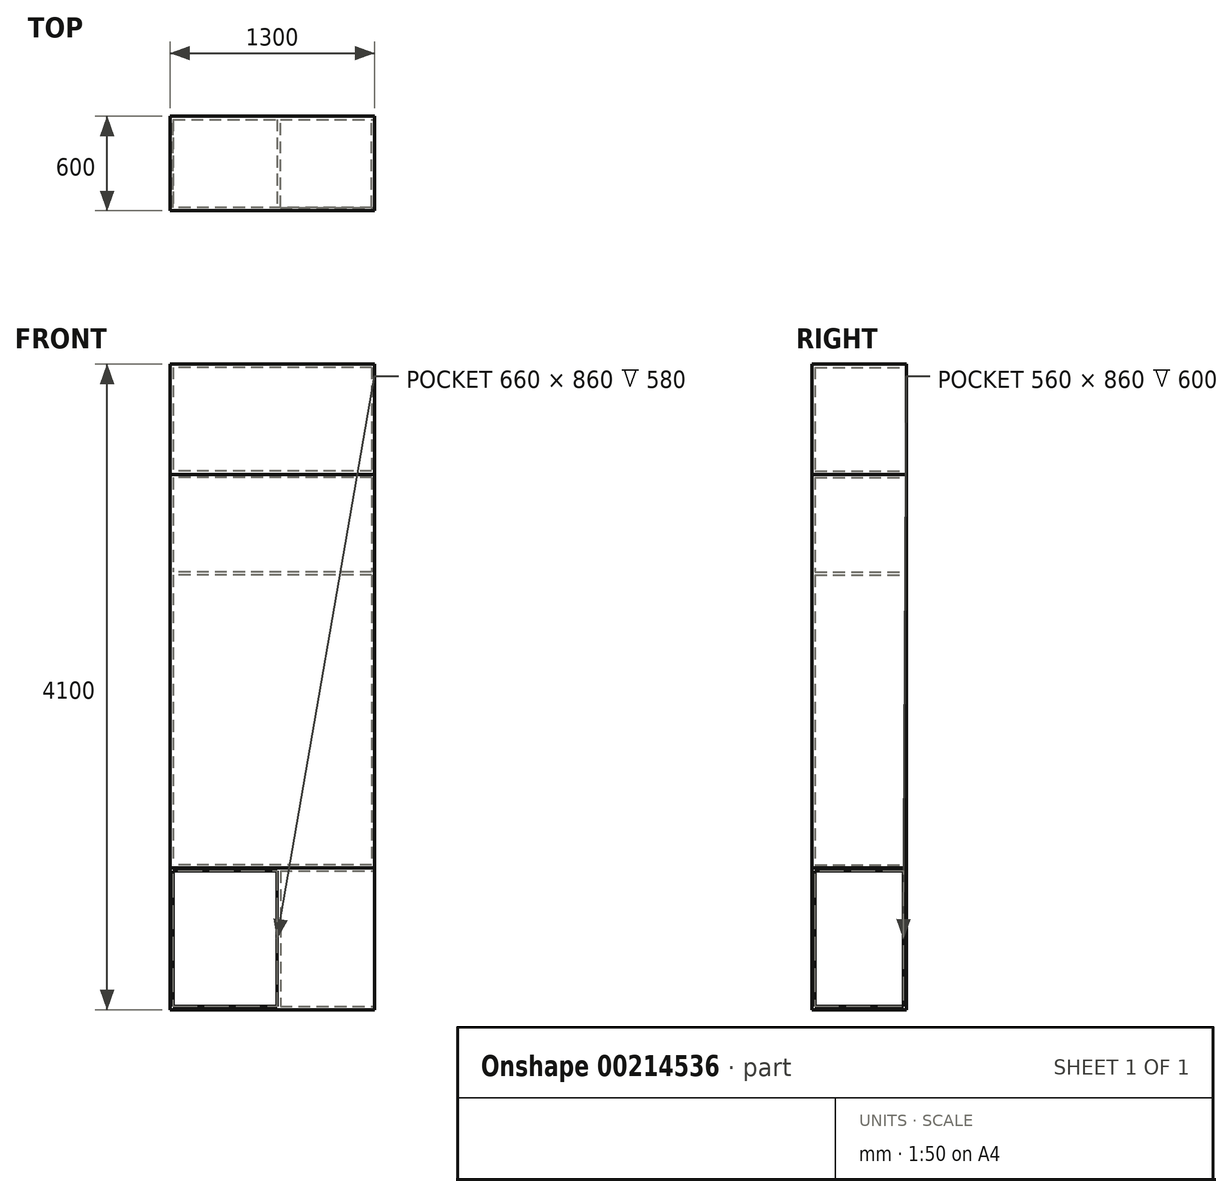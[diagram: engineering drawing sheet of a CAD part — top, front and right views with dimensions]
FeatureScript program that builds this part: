
annotation { "Feature Type Name" : "Feature", "Feature Type Description" : "" }
export const myFeature = defineFeature(function(context is Context, id is Id, definition is map)
    precondition{}
    {
        {
            var Q0;
            Q0=qCreatedBy(makeId("Top.planeOp"),FACE);
            var sketch = newSketch(context, id + "F0", { "sketchPlane" : qUnion([Q0])});
            skLineSegment(sketch, "E0.bottom", {"start": v(0, 0) * mm, "end": v(1300, 0) * mm});
            skLineSegment(sketch, "E0.top", {"start": v(0, 600) * mm, "end": v(1300, 600) * mm});
            skLineSegment(sketch, "E0.left", {"start": v(0, 0) * mm, "end": v(0, 600) * mm});
            skLineSegment(sketch, "E0.right", {"start": v(1300, 0) * mm, "end": v(1300, 600) * mm});
            skSolve(sketch);
        }
        {
            var Q0;
            Q0=makeQuery(id+"F0.imprint","IMPRINT",FACE,{"disambiguationData":[TD([[makeQuery(id+"F0.imprint","IMPRINT",EDGE,{"derivedFrom":sQuery(id+"F0.wireOp",EDGE,"E0.bottom")}),1.0]])]});
            extrude(context, id + "F1", {"entities" : qUnion([Q0]), "depth" : 900 * mm});
        }
        {
            var Q0;
            Q0=makeQuery(id+"F1.opExtrude","SWEPT_FACE",FACE,{"disambiguationData":[OSD([sQuery(id+"F0.wireOp",EDGE,"E0.right")])]});
            var sketch = newSketch(context, id + "F2", { "sketchPlane" : qUnion([Q0])});
            skLineSegment(sketch, "E1.bottom", {"start": v(20, 880) * mm, "end": v(580, 880) * mm});
            skLineSegment(sketch, "E1.top", {"start": v(20, 20) * mm, "end": v(580, 20) * mm});
            skLineSegment(sketch, "E1.left", {"start": v(20, 880) * mm, "end": v(20, 20) * mm});
            skLineSegment(sketch, "E1.right", {"start": v(580, 880) * mm, "end": v(580, 20) * mm});
            skSolve(sketch);
        }
        {
            var Q0;
            Q0 = qSketchRegion(id + "F2", true);
            extrude(context, id + "F3", {"entities" : qUnion([Q0]), "operationType" : NewBodyOperationType.REMOVE, "oppositeDirection" : true, "depth" : 600 * mm});
        }
        {
            var Q0;
            Q0=makeQuery(id+"F1.opExtrude","SWEPT_FACE",FACE,{"disambiguationData":[OSD([sQuery(id+"F0.wireOp",EDGE,"E0.bottom")])]});
            var sketch = newSketch(context, id + "F4", { "sketchPlane" : qUnion([Q0])});
            skLineSegment(sketch, "E2.bottom", {"start": v(20, 880) * mm, "end": v(680, 880) * mm});
            skLineSegment(sketch, "E2.top", {"start": v(20, 20) * mm, "end": v(680, 20) * mm});
            skLineSegment(sketch, "E2.left", {"start": v(20, 880) * mm, "end": v(20, 20) * mm});
            skLineSegment(sketch, "E2.right", {"start": v(680, 880) * mm, "end": v(680, 20) * mm});
            skSolve(sketch);
        }
        {
            var Q0;
            Q0 = qSketchRegion(id + "F4", true);
            extrude(context, id + "F5", {"entities" : qUnion([Q0]), "operationType" : NewBodyOperationType.REMOVE, "oppositeDirection" : true, "depth" : 580 * mm});
        }
        {
            var Q0;
            Q0=makeQuery(id+"F1.opExtrude","CAP_FACE",FACE,{"disambiguationData":[OSD([sQuery(id+"F0.wireOp",EDGE,"E0.bottom"),sQuery(id+"F0.wireOp",EDGE,"E0.top"),sQuery(id+"F0.wireOp",EDGE,"E0.left"),sQuery(id+"F0.wireOp",EDGE,"E0.right")])],"isStart":false});
            extrude(context, id + "F6", {"entities" : qUnion([Q0]), "depth" : 2500 * mm});
        }
        {
            var Q0;
            Q0=makeQuery(id+"F6.opExtrude","SWEPT_FACE",FACE,{"disambiguationData":[OSD([sQuery(id+"F0.wireOp",EDGE,"E0.top")])]});
            var sketch = newSketch(context, id + "F7", { "sketchPlane" : qUnion([Q0])});
            skLineSegment(sketch, "E3.bottom", {"start": v(-1280, 3380) * mm, "end": v(-20, 3380) * mm});
            skLineSegment(sketch, "E3.top", {"start": v(-1280, 2780) * mm, "end": v(-20, 2780) * mm});
            skLineSegment(sketch, "E3.left", {"start": v(-1280, 3380) * mm, "end": v(-1280, 2780) * mm});
            skLineSegment(sketch, "E3.right", {"start": v(-20, 3380) * mm, "end": v(-20, 2780) * mm});
            skSolve(sketch);
        }
        {
            var Q0;
            Q0 = qSketchRegion(id + "F7", true);
            extrude(context, id + "F8", {"entities" : qUnion([Q0]), "operationType" : NewBodyOperationType.REMOVE, "oppositeDirection" : true, "depth" : 580 * mm});
        }
        {
            var Q0;
            Q0=makeQuery(id+"F6.opExtrude","SWEPT_FACE",FACE,{"disambiguationData":[OSD([sQuery(id+"F0.wireOp",EDGE,"E0.top")])]});
            var sketch = newSketch(context, id + "F9", { "sketchPlane" : qUnion([Q0])});
            skLineSegment(sketch, "E4.bottom", {"start": v(-1280, 2760) * mm, "end": v(-20, 2760) * mm});
            skLineSegment(sketch, "E4.top", {"start": v(-1280, 920) * mm, "end": v(-20, 920) * mm});
            skLineSegment(sketch, "E4.left", {"start": v(-1280, 2760) * mm, "end": v(-1280, 920) * mm});
            skLineSegment(sketch, "E4.right", {"start": v(-20, 2760) * mm, "end": v(-20, 920) * mm});
            skSolve(sketch);
        }
        {
            var Q0;
            Q0 = qSketchRegion(id + "F9", true);
            extrude(context, id + "F10", {"entities" : qUnion([Q0]), "operationType" : NewBodyOperationType.REMOVE, "oppositeDirection" : true, "depth" : 580 * mm});
        }
        {
            var Q0;
            Q0=makeQuery(id+"F6.opExtrude","CAP_FACE",FACE,{"disambiguationData":[OSD([sQuery(id+"F0.wireOp",EDGE,"E0.bottom"),sQuery(id+"F0.wireOp",EDGE,"E0.top"),sQuery(id+"F0.wireOp",EDGE,"E0.left"),sQuery(id+"F0.wireOp",EDGE,"E0.right")])],"isStart":false});
            var sketch = newSketch(context, id + "F11", { "sketchPlane" : qUnion([Q0])});
            skLineSegment(sketch, "E5.bottom", {"start": v(1300, 0) * mm, "end": v(0, 0) * mm});
            skLineSegment(sketch, "E5.top", {"start": v(1300, 600) * mm, "end": v(0, 600) * mm});
            skLineSegment(sketch, "E5.left", {"start": v(1300, 0) * mm, "end": v(1300, 600) * mm});
            skLineSegment(sketch, "E5.right", {"start": v(0, 0) * mm, "end": v(0, 600) * mm});
            skSolve(sketch);
        }
        {
            var Q0;
            Q0 = qSketchRegion(id + "F11", true);
            extrude(context, id + "F12", {"entities" : qUnion([Q0]), "depth" : 700 * mm});
        }
        {
            var Q0;
            Q0=makeQuery(id+"F12.opExtrude","SWEPT_FACE",FACE,{"disambiguationData":[OSD([sQuery(id+"F11.wireOp",EDGE,"E5.top")])]});
            var sketch = newSketch(context, id + "F13", { "sketchPlane" : qUnion([Q0])});
            skLineSegment(sketch, "E6.bottom", {"start": v(-1280, 4080) * mm, "end": v(-20, 4080) * mm});
            skLineSegment(sketch, "E6.top", {"start": v(-1280, 3420) * mm, "end": v(-20, 3420) * mm});
            skLineSegment(sketch, "E6.left", {"start": v(-1280, 4080) * mm, "end": v(-1280, 3420) * mm});
            skLineSegment(sketch, "E6.right", {"start": v(-20, 4080) * mm, "end": v(-20, 3420) * mm});
            skSolve(sketch);
        }
        {
            var Q0;
            Q0 = qSketchRegion(id + "F13", true);
            extrude(context, id + "F14", {"entities" : qUnion([Q0]), "operationType" : NewBodyOperationType.REMOVE, "oppositeDirection" : true, "depth" : 580 * mm});
        }
    });
